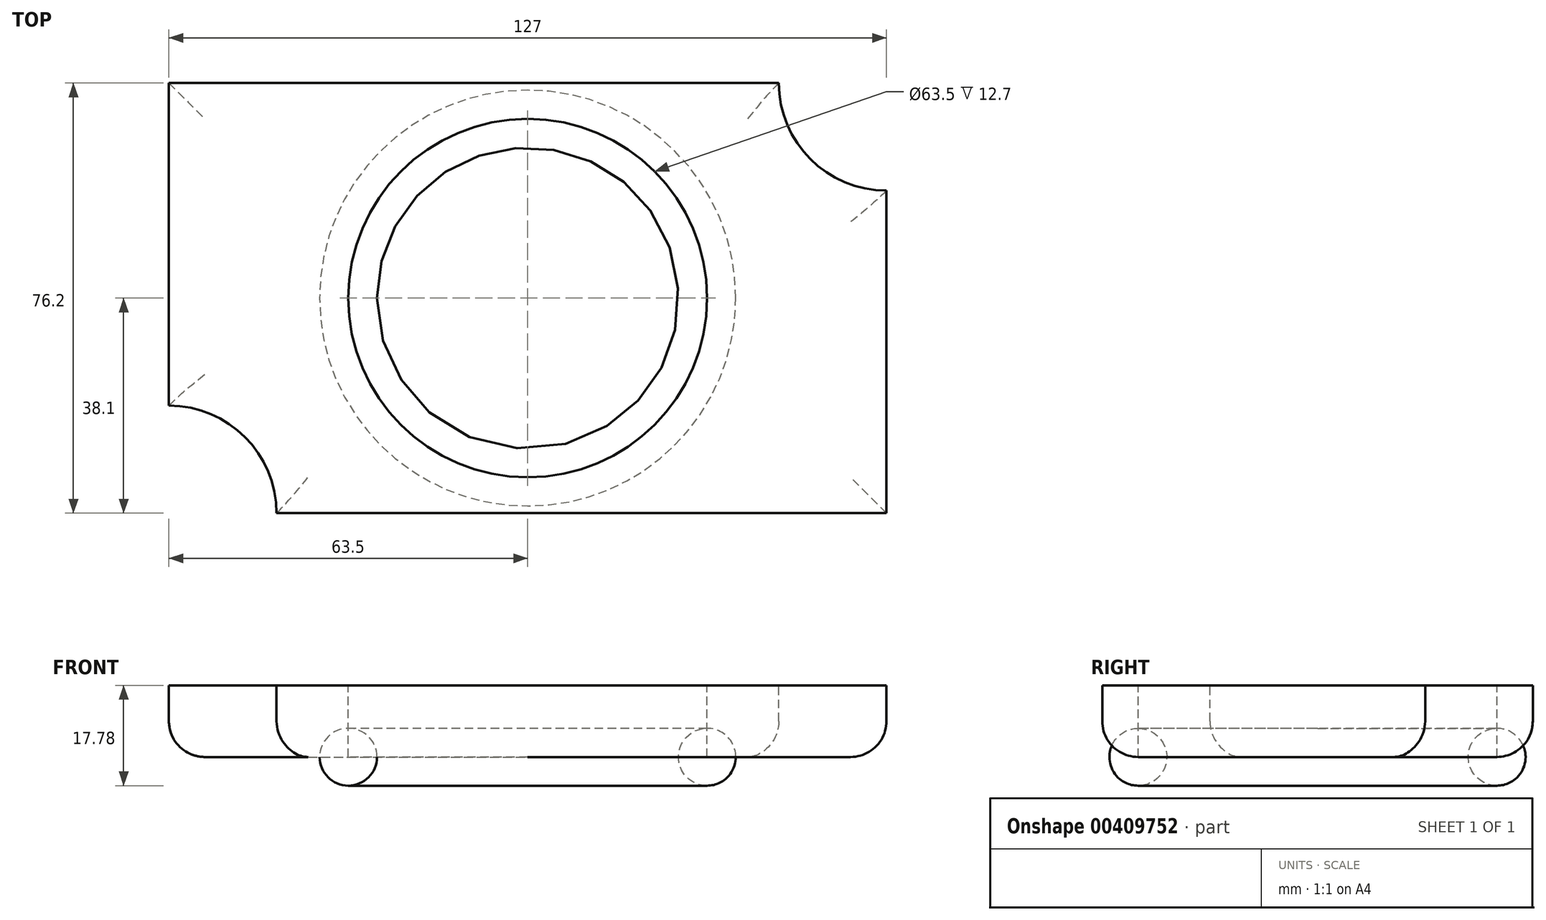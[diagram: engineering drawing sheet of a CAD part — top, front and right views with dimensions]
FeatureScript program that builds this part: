
annotation { "Feature Type Name" : "Feature", "Feature Type Description" : "" }
export const myFeature = defineFeature(function(context is Context, id is Id, definition is map)
    precondition{}
    {
        {
            var Q0;
            Q0=qCreatedBy(makeId("Top.planeOp"),FACE);
            var sketch = newSketch(context, id + "F0", { "sketchPlane" : qUnion([Q0])});
            skLineSegment(sketch, "E0.bottom", {"start": v(-63.5, -38.1) * mm, "end": v(63.5, -38.1) * mm});
            skLineSegment(sketch, "E0.top", {"start": v(-63.5, 38.1) * mm, "end": v(63.5, 38.1) * mm});
            skLineSegment(sketch, "E0.left", {"start": v(-63.5, -38.1) * mm, "end": v(-63.5, 38.1) * mm});
            skLineSegment(sketch, "E0.right", {"start": v(63.5, -38.1) * mm, "end": v(63.5, 38.1) * mm});
            skSolve(sketch);
        }
        {
            var Q0;
            Q0=makeQuery(id+"F0.imprint","IMPRINT",FACE,{"disambiguationData":[TD([[makeQuery(id+"F0.imprint","IMPRINT",EDGE,{"derivedFrom":sQuery(id+"F0.wireOp",EDGE,"E0.bottom")}),1.0]])]});
            extrude(context, id + "F1", {"entities" : qUnion([Q0]), "depth" : 12.7 * mm});
        }
        {
            var Q0;
            Q0=makeQuery(id+"F1.opExtrude","CAP_FACE",FACE,{"disambiguationData":[OSD([sQuery(id+"F0.wireOp",EDGE,"E0.bottom"),sQuery(id+"F0.wireOp",EDGE,"E0.top"),sQuery(id+"F0.wireOp",EDGE,"E0.left"),sQuery(id+"F0.wireOp",EDGE,"E0.right")])],"isStart":false});
            var sketch = newSketch(context, id + "F2", { "sketchPlane" : qUnion([Q0])});
            skCircle(sketch, "E1", {"center": v(63.5, 38.1) * mm, "radius": 19.05 * mm});
            skCircle(sketch, "E2", {"center": v(0, 0) * mm, "radius": 31.75 * mm});
            skCircle(sketch, "E3", {"center": v(-63.5, -38.1) * mm, "radius": 19.05 * mm});
            skSolve(sketch);
        }
        {
            var Q0;
            {var subQ0=sQuery(id+"F2.wireOp",EDGE,"E3");var subQ1=makeQuery(id+"F1.opExtrude","CAP_EDGE",EDGE,{"disambiguationData":[OSD([sQuery(id+"F0.wireOp",EDGE,"E0.bottom")])],"isStart":false});var subQ2=makeQuery(id+"F2.imprint","INTERSECT",VERTEX,{"derivedFrom":[subQ1,subQ0]});Q0=makeQuery(id+"F2.imprint","IMPRINT",FACE,{"disambiguationData":[TD([[makeQuery(id+"F2.imprint","IMPRINT",EDGE,{"disambiguationData":[TD([[subQ2,-1.0]])],"derivedFrom":subQ0}),1.0]])]});}
            var Q1;
            Q1=makeQuery(id+"F2.imprint","IMPRINT",FACE,{"disambiguationData":[TD([[makeQuery(id+"F2.imprint","IMPRINT",EDGE,{"derivedFrom":sQuery(id+"F2.wireOp",EDGE,"E2")}),1.0]])]});
            var Q2;
            {var subQ0=sQuery(id+"F2.wireOp",EDGE,"E1");var subQ1=makeQuery(id+"F1.opExtrude","CAP_EDGE",EDGE,{"disambiguationData":[OSD([sQuery(id+"F0.wireOp",EDGE,"E0.top")])],"isStart":false});var subQ2=makeQuery(id+"F2.imprint","INTERSECT",VERTEX,{"derivedFrom":[subQ1,subQ0]});Q2=makeQuery(id+"F2.imprint","IMPRINT",FACE,{"disambiguationData":[TD([[makeQuery(id+"F2.imprint","IMPRINT",EDGE,{"disambiguationData":[TD([[subQ2,-1.0]])],"derivedFrom":subQ0}),1.0]])]});}
            extrude(context, id + "F3", {"entities" : qUnion([Q0, Q1, Q2]), "operationType" : NewBodyOperationType.REMOVE, "endBound" : BoundingType.THROUGH_ALL, "oppositeDirection" : true, "depth" : 25.4 * mm});
        }
        {
            var Q0;
            Q0=qCreatedBy(makeId("Right.planeOp"),FACE);
            var sketch = newSketch(context, id + "F4", { "sketchPlane" : qUnion([Q0])});
            skCircle(sketch, "E4", {"center": v(-31.75, 0) * mm, "radius": 5.08 * mm});
            skLineSegment(sketch, "E5", {"start": v(0, 0) * mm, "end": v(0, 76.2) * mm, "construction": true});
            skSolve(sketch);
        }
        {
            var Q0;
            Q0=makeQuery(id+"F4.imprint","IMPRINT",FACE,{"disambiguationData":[TD([[makeQuery(id+"F4.imprint","IMPRINT",EDGE,{"derivedFrom":sQuery(id+"F4.wireOp",EDGE,"E4")}),1.0]])]});
            var Q1;
            Q1=sQuery(id+"F4.wireOp",EDGE,"E4");
            var Q2;
            Q2=sQuery(id+"F4.wireOp",EDGE,"E5");
            revolve(context, id + "F5", {"entities" : qUnion([Q0]), "surfaceEntities" : qUnion([Q1]), "axis" : qUnion([Q2]), "revolveType" : RevolveType.FULL});
        }
        {
            var Q0;
            Q0=makeQuery(id+"F1.opExtrude","CAP_EDGE",EDGE,{"disambiguationData":[OSD([sQuery(id+"F0.wireOp",EDGE,"E0.bottom")])],"isStart":true});
            var Q1;
            Q1=makeQuery(id+"F1.opExtrude","CAP_EDGE",EDGE,{"disambiguationData":[OSD([sQuery(id+"F0.wireOp",EDGE,"E0.right")])],"isStart":true});
            var Q2;
            Q2=makeQuery(id+"F3.boolean.opBoolean","INTERSECT",EDGE,{"derivedFrom":[makeQuery(id+"F1.opExtrude","CAP_FACE",FACE,{"disambiguationData":[OSD([sQuery(id+"F0.wireOp",EDGE,"E0.bottom"),sQuery(id+"F0.wireOp",EDGE,"E0.top"),sQuery(id+"F0.wireOp",EDGE,"E0.left"),sQuery(id+"F0.wireOp",EDGE,"E0.right")])],"isStart":true}),makeQuery(id+"F3.opExtrude","SWEPT_FACE",FACE,{"disambiguationData":[OSD([sQuery(id+"F2.wireOp",EDGE,"E1")])]})]});
            var Q3;
            Q3=makeQuery(id+"F1.opExtrude","CAP_EDGE",EDGE,{"disambiguationData":[OSD([sQuery(id+"F0.wireOp",EDGE,"E0.top")])],"isStart":true});
            var Q4;
            Q4=makeQuery(id+"F1.opExtrude","CAP_EDGE",EDGE,{"disambiguationData":[OSD([sQuery(id+"F0.wireOp",EDGE,"E0.left")])],"isStart":true});
            var Q5;
            Q5=makeQuery(id+"F3.boolean.opBoolean","INTERSECT",EDGE,{"derivedFrom":[makeQuery(id+"F1.opExtrude","CAP_FACE",FACE,{"disambiguationData":[OSD([sQuery(id+"F0.wireOp",EDGE,"E0.bottom"),sQuery(id+"F0.wireOp",EDGE,"E0.top"),sQuery(id+"F0.wireOp",EDGE,"E0.left"),sQuery(id+"F0.wireOp",EDGE,"E0.right")])],"isStart":true}),makeQuery(id+"F3.opExtrude","SWEPT_FACE",FACE,{"disambiguationData":[OSD([sQuery(id+"F2.wireOp",EDGE,"E3")])]})]});
            fillet(context, id + "F6", {"entities" : qUnion([Q0, Q1, Q2, Q3, Q4, Q5]), "radius" : 6.35 * mm, "tangentPropagation" : true, "allowEdgeOverflow" : false});
        }
    });
